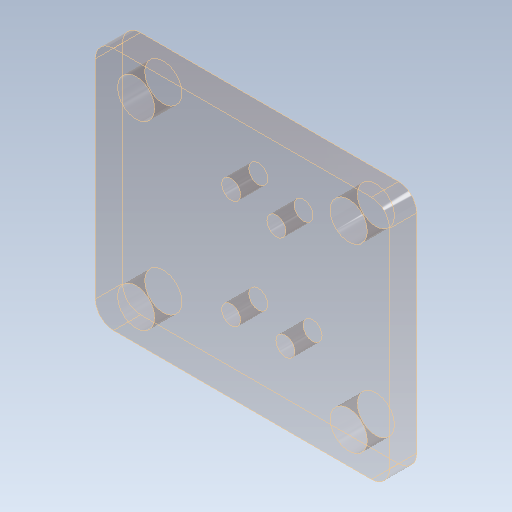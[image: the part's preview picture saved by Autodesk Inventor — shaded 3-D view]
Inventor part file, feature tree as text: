
AUTODESK INVENTOR PART (.ipt)
format: ipt  version: 2021 (Build 250183000, 183)  size: 153,600 bytes
history: native  units: mm
features: sketch x1, extrude x1, hole x1, fillet x1
ambient origin geometry x8: Origin, YZ Plane, XZ Plane, XY Plane, X Axis, Y Axis, Z Axis, Center Point
bodies: Solid1 (feature_tree)
feature tree (4):
  sketch  "Sketch1"  dims[d0=12.5mm d1=17.0mm d2=6.0mm d3=12.0mm d4=5.0mm d5=2.0mm d6=1.0mm d7=1.0mm d8=32.5mm d9=27.0mm d10=5.0mm d11=10.0mm d12=4.1mm d13=4.1mm d14=4.1mm d15=4.1mm d16=3.5mm d17=3.5mm d18=3.5mm d19=3.5mm d20=4.5mm d21=4.5mm d22=4.5mm d23=4.5mm d24=3.0mm d25=0.0mm d26=2.1mm d27=6.0mm d28=4.0mm d29=2.0mm d30=90.0deg d31=8.0mm d32=12.217305mm d33=2.0mm]
  extrude  "Extrusion1"  Depth=2.0mm
  hole  "Hole1"  [1 undecoded]
  fillet  "Fillet1"  Radius=12.0mm
note: 1 required parameter value undecoded (feature->parameter linkage not recoverable at this tier; creation-order binding heuristic only, values carry confidence <= 0.55)
